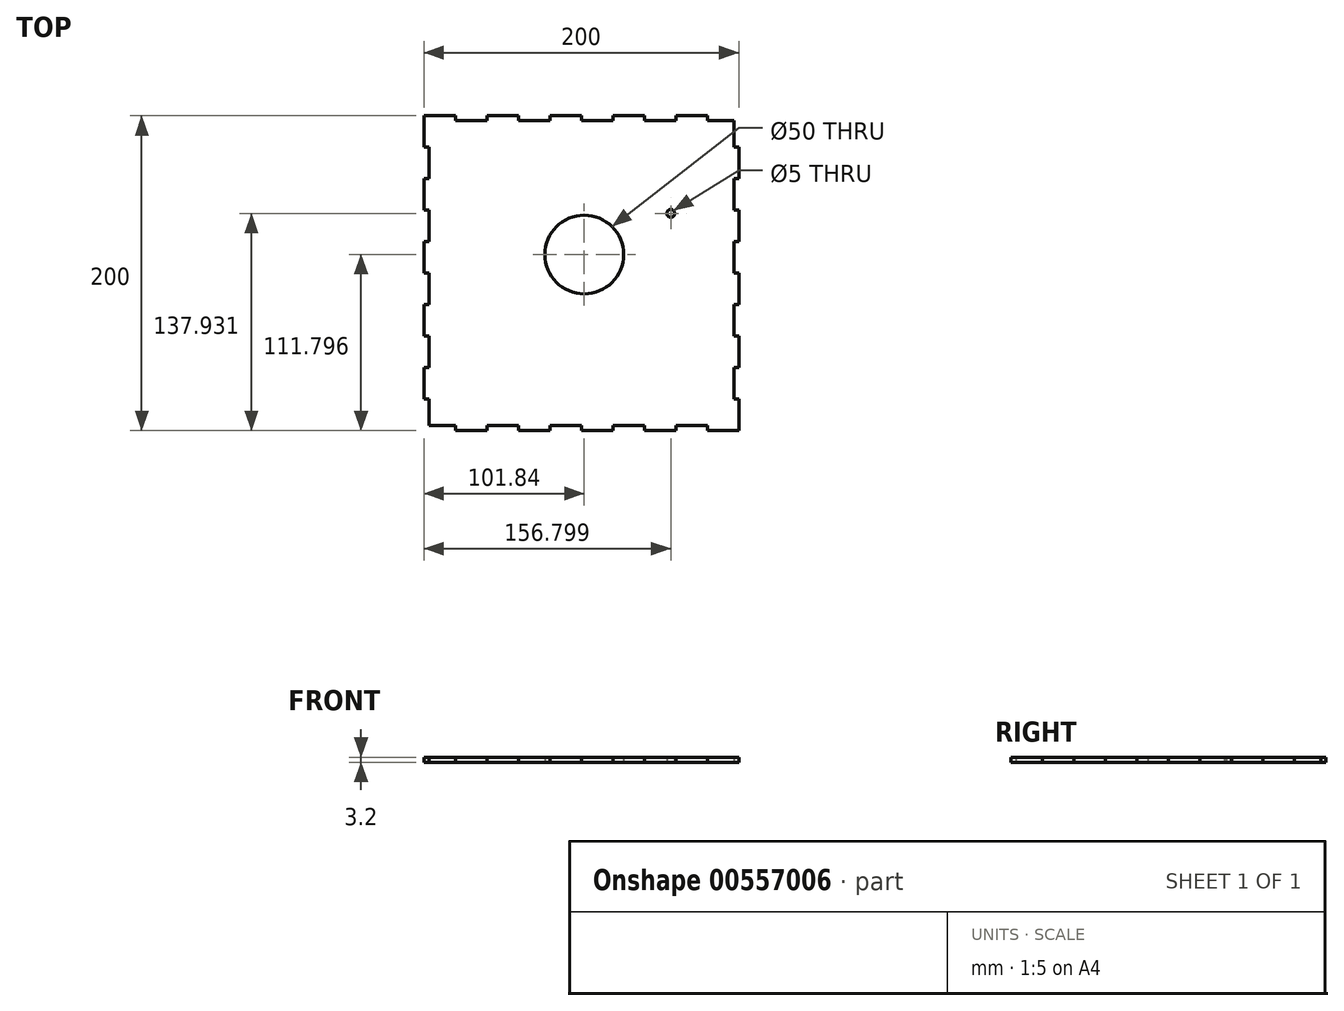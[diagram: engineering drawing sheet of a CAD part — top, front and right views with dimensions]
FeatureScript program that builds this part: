
annotation { "Feature Type Name" : "Feature", "Feature Type Description" : "" }
export const myFeature = defineFeature(function(context is Context, id is Id, definition is map)
    precondition{}
    {
        {
            var Q0;
            Q0=qCreatedBy(makeId("Top.planeOp"),FACE);
            var sketch = newSketch(context, id + "F0", { "sketchPlane" : qUnion([Q0])});
            skLineSegment(sketch, "E0.bottom", {"start": v(-101.84, 101.83) * mm, "end": v(-81.84, 101.83) * mm});
            skLineSegment(sketch, "E0.top", {"start": v(-81.84, -98.17) * mm, "end": v(-61.84, -98.17) * mm});
            skLineSegment(sketch, "E0.left", {"start": v(-101.84, 101.83) * mm, "end": v(-101.84, 81.83) * mm});
            skLineSegment(sketch, "E0.right", {"start": v(98.16, 81.83) * mm, "end": v(98.16, 61.83) * mm});
            skLineSegment(sketch, "E1.bottom", {"start": v(-98.64, -94.97) * mm, "end": v(-81.84, -94.97) * mm});
            skLineSegment(sketch, "E1.right", {"start": v(-81.84, -94.97) * mm, "end": v(-81.84, -98.17) * mm});
            skLineSegment(sketch, "E2.bottom", {"start": v(-61.84, -94.97) * mm, "end": v(-41.84, -94.97) * mm});
            skLineSegment(sketch, "E2.left", {"start": v(-61.84, -94.97) * mm, "end": v(-61.84, -98.17) * mm});
            skLineSegment(sketch, "E2.right", {"start": v(-41.84, -94.97) * mm, "end": v(-41.84, -98.17) * mm});
            skLineSegment(sketch, "E3.bottom", {"start": v(-21.84, -94.97) * mm, "end": v(-1.84, -94.97) * mm});
            skLineSegment(sketch, "E3.left", {"start": v(-21.84, -94.97) * mm, "end": v(-21.84, -98.17) * mm});
            skLineSegment(sketch, "E3.right", {"start": v(-1.84, -94.97) * mm, "end": v(-1.84, -98.17) * mm});
            skLineSegment(sketch, "E4.bottom", {"start": v(18.16, -94.97) * mm, "end": v(38.16, -94.97) * mm});
            skLineSegment(sketch, "E4.left", {"start": v(18.16, -94.97) * mm, "end": v(18.16, -98.17) * mm});
            skLineSegment(sketch, "E4.right", {"start": v(38.16, -94.97) * mm, "end": v(38.16, -98.17) * mm});
            skLineSegment(sketch, "E5.bottom", {"start": v(58.16, -94.97) * mm, "end": v(78.16, -94.97) * mm});
            skLineSegment(sketch, "E5.left", {"start": v(58.16, -94.97) * mm, "end": v(58.16, -98.17) * mm});
            skLineSegment(sketch, "E5.right", {"start": v(78.16, -94.97) * mm, "end": v(78.16, -98.17) * mm});
            skLineSegment(sketch, "E6.trimOffspring", {"start": v(-41.84, -98.17) * mm, "end": v(-21.84, -98.17) * mm});
            skLineSegment(sketch, "E7.trimOffspring", {"start": v(-1.84, -98.17) * mm, "end": v(18.16, -98.17) * mm});
            skLineSegment(sketch, "E8.trimOffspring", {"start": v(38.16, -98.17) * mm, "end": v(58.16, -98.17) * mm});
            skLineSegment(sketch, "E9.trimOffspring", {"start": v(78.16, -98.17) * mm, "end": v(98.16, -98.17) * mm});
            skLineSegment(sketch, "E10.bottom", {"start": v(94.96, -58.17) * mm, "end": v(98.16, -58.17) * mm});
            skLineSegment(sketch, "E10.top", {"start": v(94.96, -78.17) * mm, "end": v(98.16, -78.17) * mm});
            skLineSegment(sketch, "E10.left", {"start": v(94.96, -58.17) * mm, "end": v(94.96, -78.17) * mm});
            skLineSegment(sketch, "E11.bottom", {"start": v(94.96, -18.17) * mm, "end": v(98.16, -18.17) * mm});
            skLineSegment(sketch, "E11.top", {"start": v(94.96, -38.17) * mm, "end": v(98.16, -38.17) * mm});
            skLineSegment(sketch, "E11.left", {"start": v(94.96, -18.17) * mm, "end": v(94.96, -38.17) * mm});
            skLineSegment(sketch, "E12.bottom", {"start": v(94.96, 21.83) * mm, "end": v(98.16, 21.83) * mm});
            skLineSegment(sketch, "E12.top", {"start": v(94.96, 1.83) * mm, "end": v(98.16, 1.83) * mm});
            skLineSegment(sketch, "E12.left", {"start": v(94.96, 21.83) * mm, "end": v(94.96, 1.83) * mm});
            skLineSegment(sketch, "E13.bottom", {"start": v(94.96, 61.83) * mm, "end": v(98.16, 61.83) * mm});
            skLineSegment(sketch, "E13.top", {"start": v(94.96, 41.83) * mm, "end": v(98.16, 41.83) * mm});
            skLineSegment(sketch, "E13.left", {"start": v(94.96, 61.83) * mm, "end": v(94.96, 41.83) * mm});
            skLineSegment(sketch, "E14.top", {"start": v(94.96, 81.83) * mm, "end": v(98.16, 81.83) * mm});
            skLineSegment(sketch, "E14.left", {"start": v(94.96, 98.63) * mm, "end": v(94.96, 81.83) * mm});
            skLineSegment(sketch, "E15.trimOffspring", {"start": v(98.16, 41.83) * mm, "end": v(98.16, 21.83) * mm});
            skLineSegment(sketch, "E16.trimOffspring", {"start": v(98.16, 1.83) * mm, "end": v(98.16, -18.17) * mm});
            skLineSegment(sketch, "E17.trimOffspring", {"start": v(98.16, -38.17) * mm, "end": v(98.16, -58.17) * mm});
            skLineSegment(sketch, "E18.trimOffspring", {"start": v(98.16, -78.17) * mm, "end": v(98.16, -98.17) * mm});
            skLineSegment(sketch, "E19.top", {"start": v(78.16, 98.63) * mm, "end": v(94.96, 98.63) * mm});
            skLineSegment(sketch, "E19.left", {"start": v(78.16, 101.83) * mm, "end": v(78.16, 98.63) * mm});
            skLineSegment(sketch, "E20.top", {"start": v(38.16, 98.63) * mm, "end": v(58.16, 98.63) * mm});
            skLineSegment(sketch, "E20.left", {"start": v(38.16, 101.83) * mm, "end": v(38.16, 98.63) * mm});
            skLineSegment(sketch, "E20.right", {"start": v(58.16, 101.83) * mm, "end": v(58.16, 98.63) * mm});
            skLineSegment(sketch, "E21.top", {"start": v(-1.84, 98.63) * mm, "end": v(18.16, 98.63) * mm});
            skLineSegment(sketch, "E21.left", {"start": v(-1.84, 101.83) * mm, "end": v(-1.84, 98.63) * mm});
            skLineSegment(sketch, "E21.right", {"start": v(18.16, 101.83) * mm, "end": v(18.16, 98.63) * mm});
            skLineSegment(sketch, "E22.top", {"start": v(-41.84, 98.63) * mm, "end": v(-21.84, 98.63) * mm});
            skLineSegment(sketch, "E22.left", {"start": v(-41.84, 101.83) * mm, "end": v(-41.84, 98.63) * mm});
            skLineSegment(sketch, "E22.right", {"start": v(-21.84, 101.83) * mm, "end": v(-21.84, 98.63) * mm});
            skLineSegment(sketch, "E23.top", {"start": v(-81.84, 98.63) * mm, "end": v(-61.84, 98.63) * mm});
            skLineSegment(sketch, "E23.left", {"start": v(-81.84, 101.83) * mm, "end": v(-81.84, 98.63) * mm});
            skLineSegment(sketch, "E23.right", {"start": v(-61.84, 101.83) * mm, "end": v(-61.84, 98.63) * mm});
            skLineSegment(sketch, "E24.trimOffspring", {"start": v(-61.84, 101.83) * mm, "end": v(-41.84, 101.83) * mm});
            skLineSegment(sketch, "E25.trimOffspring", {"start": v(-21.84, 101.83) * mm, "end": v(-1.84, 101.83) * mm});
            skLineSegment(sketch, "E26.trimOffspring", {"start": v(18.16, 101.83) * mm, "end": v(38.16, 101.83) * mm});
            skLineSegment(sketch, "E27.trimOffspring", {"start": v(58.16, 101.83) * mm, "end": v(78.16, 101.83) * mm});
            skLineSegment(sketch, "E28.bottom", {"start": v(-101.84, 81.83) * mm, "end": v(-98.64, 81.83) * mm});
            skLineSegment(sketch, "E28.top", {"start": v(-101.84, 61.83) * mm, "end": v(-98.64, 61.83) * mm});
            skLineSegment(sketch, "E28.right", {"start": v(-98.64, 81.83) * mm, "end": v(-98.64, 61.83) * mm});
            skLineSegment(sketch, "E29.bottom", {"start": v(-101.84, 41.83) * mm, "end": v(-98.64, 41.83) * mm});
            skLineSegment(sketch, "E29.top", {"start": v(-101.84, 21.83) * mm, "end": v(-98.64, 21.83) * mm});
            skLineSegment(sketch, "E29.right", {"start": v(-98.64, 41.83) * mm, "end": v(-98.64, 21.83) * mm});
            skLineSegment(sketch, "E30.bottom", {"start": v(-101.84, 1.83) * mm, "end": v(-98.64, 1.83) * mm});
            skLineSegment(sketch, "E30.top", {"start": v(-101.84, -18.17) * mm, "end": v(-98.64, -18.17) * mm});
            skLineSegment(sketch, "E30.right", {"start": v(-98.64, 1.83) * mm, "end": v(-98.64, -18.17) * mm});
            skLineSegment(sketch, "E31.left", {"start": v(-101.84, -58.17) * mm, "end": v(-101.84, -78.17) * mm});
            skPoint(sketch, "E32.trimOffspring.end.orphan", {"position": v(98.16, 101.83) * mm});
            skPoint(sketch, "E14.bottom.start.orphan", {"position": v(94.96, 101.83) * mm});
            skLineSegment(sketch, "E33.bottom", {"start": v(-101.84, -38.17) * mm, "end": v(-98.64, -38.17) * mm});
            skLineSegment(sketch, "E33.top", {"start": v(-101.84, -58.17) * mm, "end": v(-98.64, -58.17) * mm});
            skLineSegment(sketch, "E33.right", {"start": v(-98.64, -38.17) * mm, "end": v(-98.64, -58.17) * mm});
            skLineSegment(sketch, "E34.bottom", {"start": v(-101.84, -78.17) * mm, "end": v(-98.64, -78.17) * mm});
            skLineSegment(sketch, "E34.right", {"start": v(-98.64, -78.17) * mm, "end": v(-98.64, -94.97) * mm});
            skPoint(sketch, "E1.left.end.orphan", {"position": v(-101.84, -98.17) * mm});
            skLineSegment(sketch, "E35.trimOffspring", {"start": v(-101.84, -18.17) * mm, "end": v(-101.84, -38.17) * mm});
            skLineSegment(sketch, "E36.trimOffspring", {"start": v(-101.84, 21.83) * mm, "end": v(-101.84, 1.83) * mm});
            skLineSegment(sketch, "E37.trimOffspring", {"start": v(-101.84, 61.83) * mm, "end": v(-101.84, 41.83) * mm});
            skCircle(sketch, "E38", {"center": v(0, 13.63) * mm, "radius": 25 * mm});
            skCircle(sketch, "E39", {"center": v(54.96, 39.76) * mm, "radius": 2.5 * mm});
            skSolve(sketch);
        }
        {
            var Q0;
            Q0=qSketchRegion(id+"F0",true);
            extrude(context, id + "F1", {"entities" : qUnion([Q0]), "depth" : 3.2 * mm});
        }
    });
